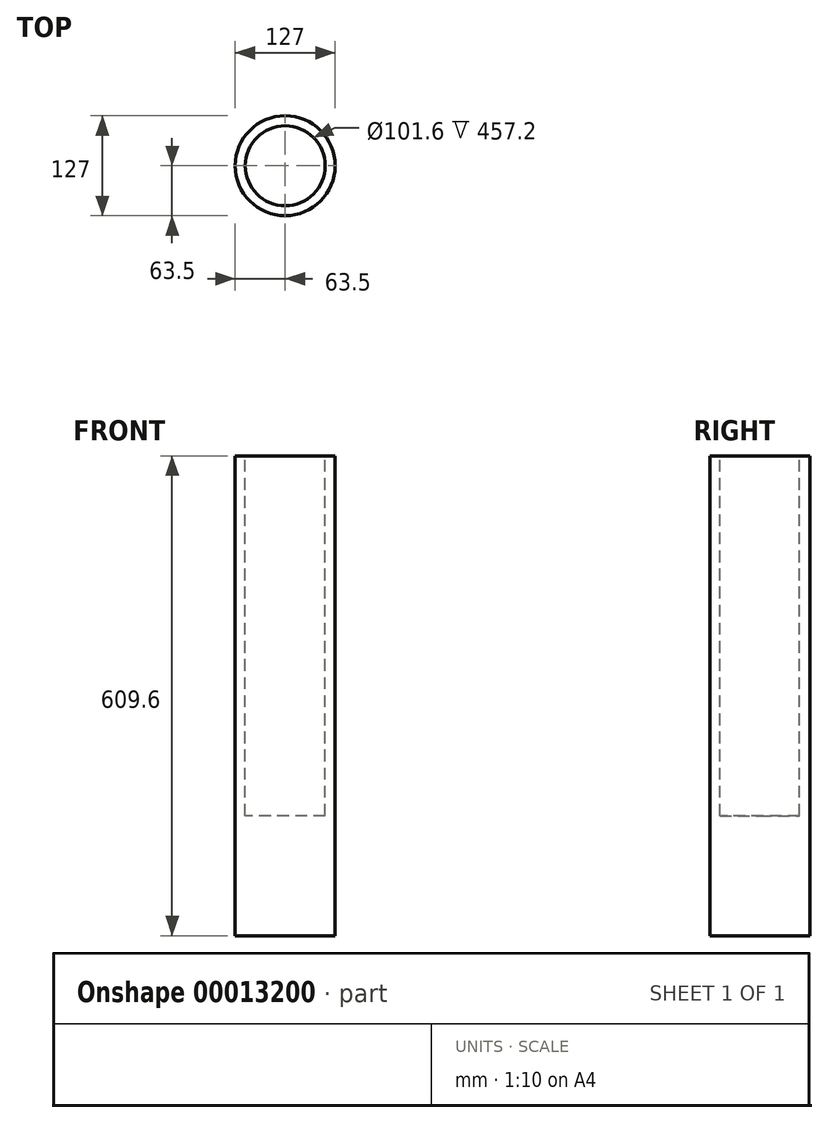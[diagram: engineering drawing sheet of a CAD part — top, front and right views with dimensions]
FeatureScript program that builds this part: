
annotation { "Feature Type Name" : "Feature", "Feature Type Description" : "" }
export const myFeature = defineFeature(function(context is Context, id is Id, definition is map)
    precondition{}
    {
        {
            var Q0;
            Q0=qCreatedBy(makeId("Top.planeOp"),FACE);
            var sketch = newSketch(context, id + "F0", { "sketchPlane" : qUnion([Q0])});
            skCircle(sketch, "E0", {"center": v(0, 0) * mm, "radius": 63.5 * mm});
            skSolve(sketch);
        }
        {
            var Q0;
            Q0 = qSketchRegion(id + "F0", true);
            var Q1;
            Q1 = qSketchRegion(id + "F2", true);
            extrude(context, id + "F1", {"entities" : qUnion([Q0, Q1]), "depth" : 609.6 * mm});
        }
        {
            var Q0;
            Q0=makeQuery(id+"F1.opExtrude","CAP_FACE",FACE,{"disambiguationData":[OSD([sQuery(id+"F0.wireOp",EDGE,"E0")])],"isStart":false});
            var sketch = newSketch(context, id + "F2", { "sketchPlane" : qUnion([Q0])});
            skCircle(sketch, "E1", {"center": v(0, 0) * mm, "radius": 50.8 * mm});
            skSolve(sketch);
        }
        {
            var Q0;
            Q0 = qSketchRegion(id + "F2", true);
            extrude(context, id + "F3", {"entities" : qUnion([Q0]), "operationType" : NewBodyOperationType.REMOVE, "oppositeDirection" : true, "depth" : 457.2 * mm});
        }
    });
